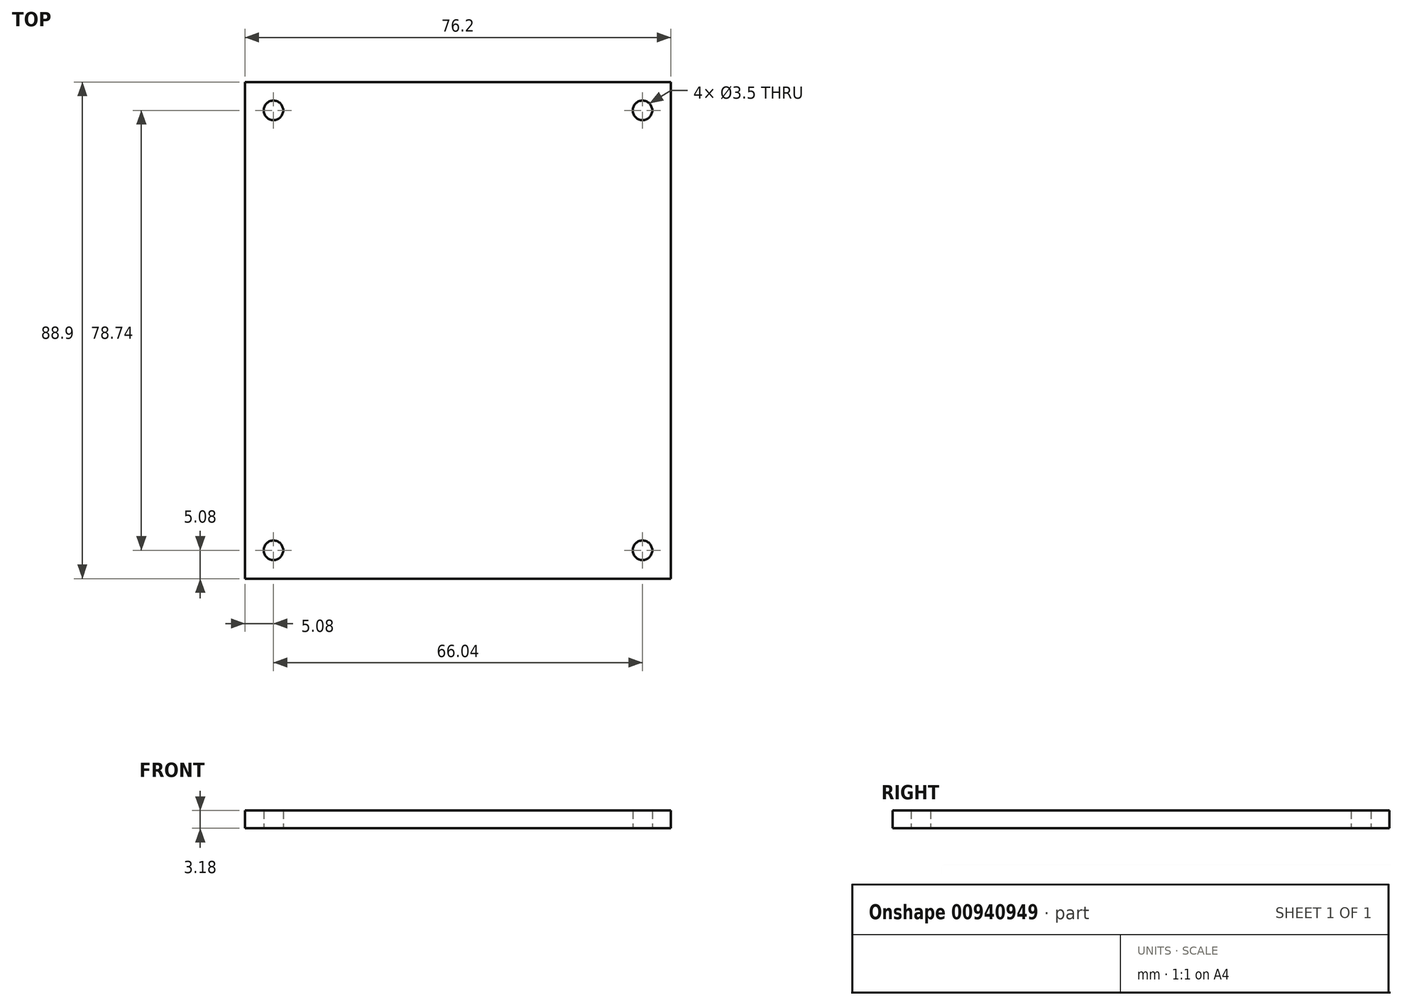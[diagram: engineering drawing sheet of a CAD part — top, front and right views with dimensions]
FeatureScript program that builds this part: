
annotation { "Feature Type Name" : "Feature", "Feature Type Description" : "" }
export const myFeature = defineFeature(function(context is Context, id is Id, definition is map)
    precondition{}
    {
        {
            var Q0;
            Q0=qCreatedBy(makeId("Top.planeOp"),FACE);
            var sketch = newSketch(context, id + "F0", { "sketchPlane" : qUnion([Q0])});
            skLineSegment(sketch, "E0.bottom", {"start": v(0, 0) * mm, "end": v(76.2, 0) * mm});
            skLineSegment(sketch, "E0.top", {"start": v(0, 88.9) * mm, "end": v(76.2, 88.9) * mm});
            skLineSegment(sketch, "E0.left", {"start": v(0, 0) * mm, "end": v(0, 88.9) * mm});
            skLineSegment(sketch, "E0.right", {"start": v(76.2, 0) * mm, "end": v(76.2, 88.9) * mm});
            skLineSegment(sketch, "E1.bottom", {"start": v(5.08, 83.82) * mm, "end": v(71.12, 83.82) * mm, "construction": true});
            skLineSegment(sketch, "E1.top", {"start": v(5.08, 5.08) * mm, "end": v(71.12, 5.08) * mm, "construction": true});
            skLineSegment(sketch, "E1.left", {"start": v(5.08, 83.82) * mm, "end": v(5.08, 5.08) * mm, "construction": true});
            skLineSegment(sketch, "E1.right", {"start": v(71.12, 83.82) * mm, "end": v(71.12, 5.08) * mm, "construction": true});
            skLineSegment(sketch, "E2", {"start": v(38.1, 88.9) * mm, "end": v(38.1, 83.82) * mm, "construction": true});
            skPoint(sketch, "E2.endSnap0", {"position": v(38.1, 83.82) * mm});
            skLineSegment(sketch, "E3", {"start": v(0, 44.45) * mm, "end": v(5.08, 44.45) * mm, "construction": true});
            skLineSegment(sketch, "E4", {"start": v(38.1, 5.08) * mm, "end": v(38.1, 0) * mm, "construction": true});
            skLineSegment(sketch, "E5", {"start": v(71.12, 44.45) * mm, "end": v(76.2, 44.45) * mm, "construction": true});
            skCircle(sketch, "E6", {"center": v(5.08, 83.82) * mm, "radius": 1.75 * mm});
            skCircle(sketch, "E7", {"center": v(71.12, 83.82) * mm, "radius": 1.75 * mm});
            skCircle(sketch, "E8", {"center": v(71.12, 5.08) * mm, "radius": 1.75 * mm});
            skCircle(sketch, "E9", {"center": v(5.08, 5.08) * mm, "radius": 1.75 * mm});
            skSolve(sketch);
        }
        {
            var Q0;
            Q0 = qSketchRegion(id + "F0", true);
            extrude(context, id + "F1", {"entities" : qUnion([Q0]), "depth" : 3.17 * mm, "offsetDistance" : 25.4 * mm});
        }
    });
